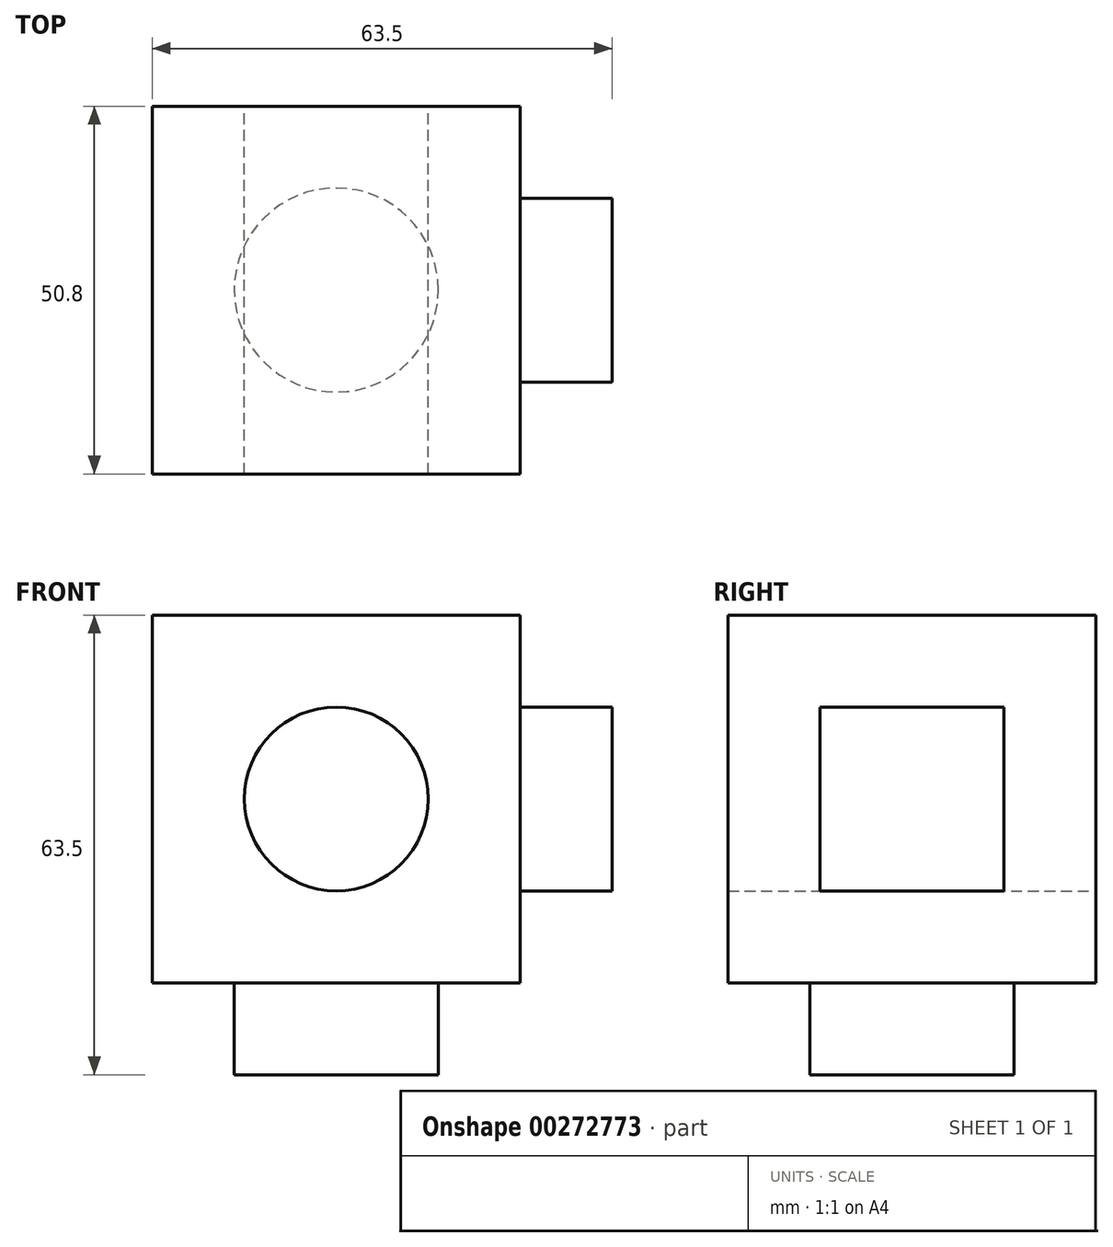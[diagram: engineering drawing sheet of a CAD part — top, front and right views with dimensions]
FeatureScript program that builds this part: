
annotation { "Feature Type Name" : "Feature", "Feature Type Description" : "" }
export const myFeature = defineFeature(function(context is Context, id is Id, definition is map)
    precondition{}
    {
        {
            var Q0;
            Q0=qCreatedBy(makeId("Front.planeOp"),FACE);
            var sketch = newSketch(context, id + "F0", { "sketchPlane" : qUnion([Q0])});
            skLineSegment(sketch, "E0.bottom", {"start": v(0, 0) * mm, "end": v(-50.8, 0) * mm});
            skLineSegment(sketch, "E0.top", {"start": v(0, 50.8) * mm, "end": v(-50.8, 50.8) * mm});
            skLineSegment(sketch, "E0.left", {"start": v(0, 0) * mm, "end": v(0, 50.8) * mm});
            skLineSegment(sketch, "E0.right", {"start": v(-50.8, 0) * mm, "end": v(-50.8, 50.8) * mm});
            skSolve(sketch);
        }
        {
            var Q0;
            Q0=makeQuery(id+"F0.imprint","IMPRINT",FACE,{"disambiguationData":[TD([[makeQuery(id+"F0.imprint","IMPRINT",EDGE,{"derivedFrom":sQuery(id+"F0.wireOp",EDGE,"E0.bottom")}),-1.0]])]});
            var sketch = newSketch(context, id + "F1", { "sketchPlane" : qUnion([Q0])});
            skCircle(sketch, "E1", {"center": v(-25.4, 25.4) * mm, "radius": 12.7 * mm});
            skSolve(sketch);
        }
        {
            var Q0;
            Q0=makeQuery(id+"F0.imprint","IMPRINT",FACE,{"disambiguationData":[TD([[makeQuery(id+"F0.imprint","IMPRINT",EDGE,{"derivedFrom":sQuery(id+"F0.wireOp",EDGE,"E0.bottom")}),-1.0]])]});
            extrude(context, id + "F2", {"entities" : qUnion([Q0]), "depth" : 50.8 * mm});
        }
        {
            var Q0;
            Q0 = qSketchRegion(id + "F1", true);
            extrude(context, id + "F3", {"entities" : qUnion([Q0]), "operationType" : NewBodyOperationType.REMOVE, "depth" : 51.3 * mm});
        }
        {
            var Q0;
            Q0=makeQuery(id+"F2.opExtrude","SWEPT_FACE",FACE,{"disambiguationData":[OSD([sQuery(id+"F0.wireOp",EDGE,"E0.left")])]});
            var sketch = newSketch(context, id + "F4", { "sketchPlane" : qUnion([Q0])});
            skLineSegment(sketch, "E2.bottom", {"start": v(-38.1, 38.1) * mm, "end": v(-12.7, 38.1) * mm});
            skLineSegment(sketch, "E2.top", {"start": v(-38.1, 12.7) * mm, "end": v(-12.7, 12.7) * mm});
            skLineSegment(sketch, "E2.left", {"start": v(-38.1, 38.1) * mm, "end": v(-38.1, 12.7) * mm});
            skLineSegment(sketch, "E2.right", {"start": v(-12.7, 38.1) * mm, "end": v(-12.7, 12.7) * mm});
            skSolve(sketch);
        }
        {
            var Q0;
            Q0 = qSketchRegion(id + "F4", true);
            extrude(context, id + "F5", {"entities" : qUnion([Q0]), "operationType" : NewBodyOperationType.ADD, "depth" : 12.7 * mm});
        }
        {
            var Q0;
            Q0=makeQuery(id+"F2.opExtrude","SWEPT_FACE",FACE,{"disambiguationData":[OSD([sQuery(id+"F0.wireOp",EDGE,"E0.bottom")])]});
            var sketch = newSketch(context, id + "F6", { "sketchPlane" : qUnion([Q0])});
            skCircle(sketch, "E3", {"center": v(-25.4, 25.4) * mm, "radius": 14.1 * mm});
            skSolve(sketch);
        }
        {
            var Q0;
            Q0 = qSketchRegion(id + "F6", true);
            extrude(context, id + "F7", {"entities" : qUnion([Q0]), "operationType" : NewBodyOperationType.ADD, "depth" : 12.7 * mm});
        }
    });
